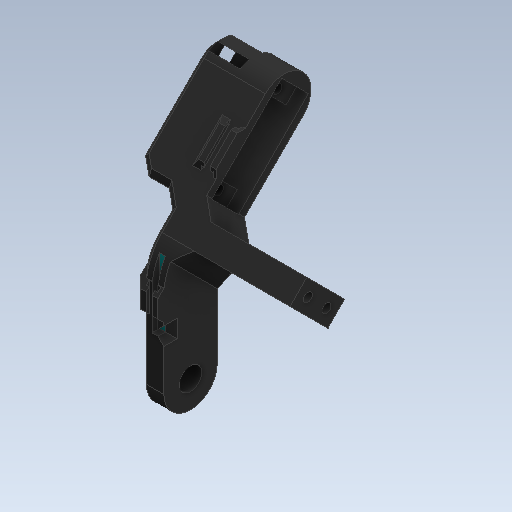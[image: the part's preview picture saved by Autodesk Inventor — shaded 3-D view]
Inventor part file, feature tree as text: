
AUTODESK INVENTOR PART (.ipt)
format: ipt  version: 2020 (Build 240168000, 168)  size: 415,744 bytes
history: native  units: in
note: dims shown in document units (in); Inventor stores cm internally (conversion verified against a paired STEP export)
features: sketch x22, other x7, plane x4
ambient origin geometry x8: Origin, YZ Plane, XZ Plane, XY Plane, X Axis, Y Axis, Z Axis, Center Point
bodies: Solid2 (feature_tree), Solid3 (feature_tree), Solid1 (feature_tree), Solid4 (feature_tree)
feature tree (33):
  other  "PatellaBot.ipt"
  other  "Solid1::PatellaBot.ipt"
  other  "Solid4::PatellaBot.ipt"
  other  "Solid5::PatellaBot.ipt"
  other  "Solid2::PatellaBot.ipt"
  other  "Solid3::PatellaBot.ipt"
  other  "TaggingFeature1"
  sketch  "Sketch1"  dims[d0=0.3937in]
  sketch  "Sketch2"
  sketch  "Sketch3"
  sketch  "Sketch4"
  sketch  "Sketch5"
  sketch  "Sketch12"
  sketch  "Sketch14"
  sketch  "Sketch15"
  sketch  "Sketch16"
  sketch  "Sketch17"
  sketch  "Sketch19"
  sketch  "Sketch22"
  sketch  "Sketch23"
  sketch  "Sketch25"
  sketch  "Sketch26"
  sketch  "Sketch27"
  sketch  "Sketch28"
  sketch  "Sketch32"
  sketch  "Sketch33"
  sketch  "Sketch39"
  sketch  "Sketch40"
  sketch  "Sketch46"
  plane  "Work Plane1"
  plane  "Work Plane2"
  plane  "Work Plane3"
  plane  "Work Plane4"
